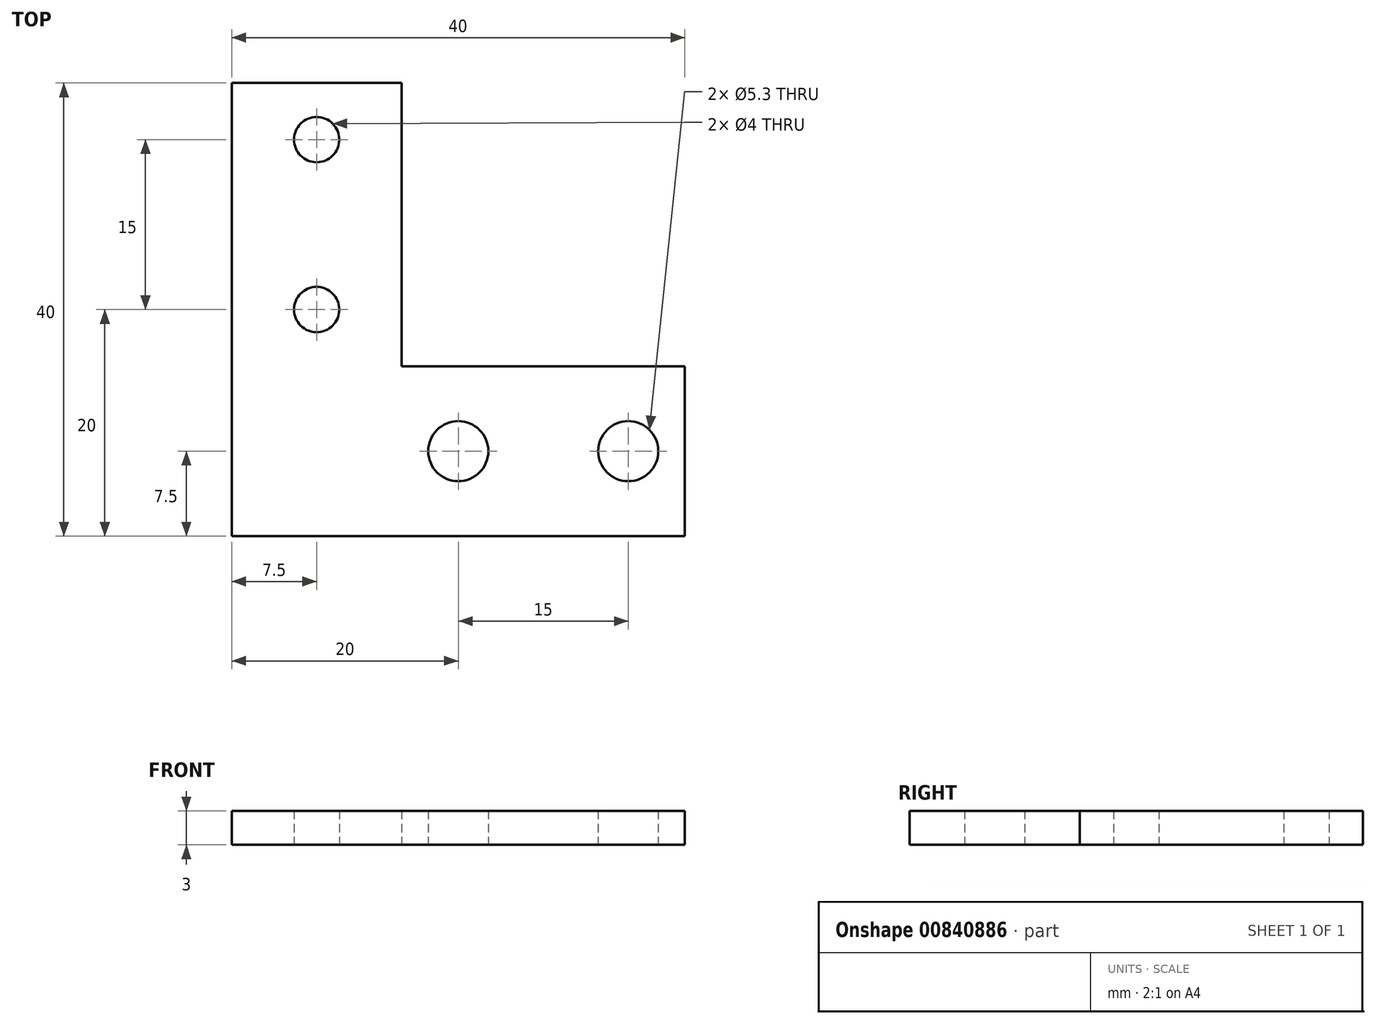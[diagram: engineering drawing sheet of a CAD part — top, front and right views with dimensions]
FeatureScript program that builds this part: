
annotation { "Feature Type Name" : "Feature", "Feature Type Description" : "" }
export const myFeature = defineFeature(function(context is Context, id is Id, definition is map)
    precondition{}
    {
        {
            var Q0;
            Q0=qCreatedBy(makeId("Top.planeOp"),FACE);
            var sketch = newSketch(context, id + "F0", { "sketchPlane" : qUnion([Q0])});
            skLineSegment(sketch, "E0", {"start": v(0, 0) * mm, "end": v(0, 40) * mm});
            skLineSegment(sketch, "E1", {"start": v(0, 40) * mm, "end": v(15, 40) * mm});
            skLineSegment(sketch, "E2", {"start": v(15, 40) * mm, "end": v(15, 15) * mm});
            skLineSegment(sketch, "E3", {"start": v(15, 15) * mm, "end": v(40, 15) * mm});
            skLineSegment(sketch, "E4", {"start": v(40, 15) * mm, "end": v(40, 0) * mm});
            skLineSegment(sketch, "E5", {"start": v(40, 0) * mm, "end": v(0, 0) * mm});
            skCircle(sketch, "E6", {"center": v(7.5, 35) * mm, "radius": 2 * mm});
            skPoint(sketch, "E6.centerSnap0", {"position": v(7.5, 40) * mm});
            skCircle(sketch, "E7", {"center": v(7.5, 20) * mm, "radius": 2 * mm});
            skCircle(sketch, "E8", {"center": v(35, 7.5) * mm, "radius": 2.65 * mm});
            skPoint(sketch, "E8.centerSnap0", {"position": v(40, 7.5) * mm});
            skCircle(sketch, "E9", {"center": v(20, 7.5) * mm, "radius": 2.65 * mm});
            skSolve(sketch);
        }
        {
            var Q0;
            Q0=qSketchRegion(id+"F0",true);
            extrude(context, id + "F1", {"entities" : qUnion([Q0]), "depth" : 3 * mm, "offsetDistance" : 25 * mm});
        }
    });
